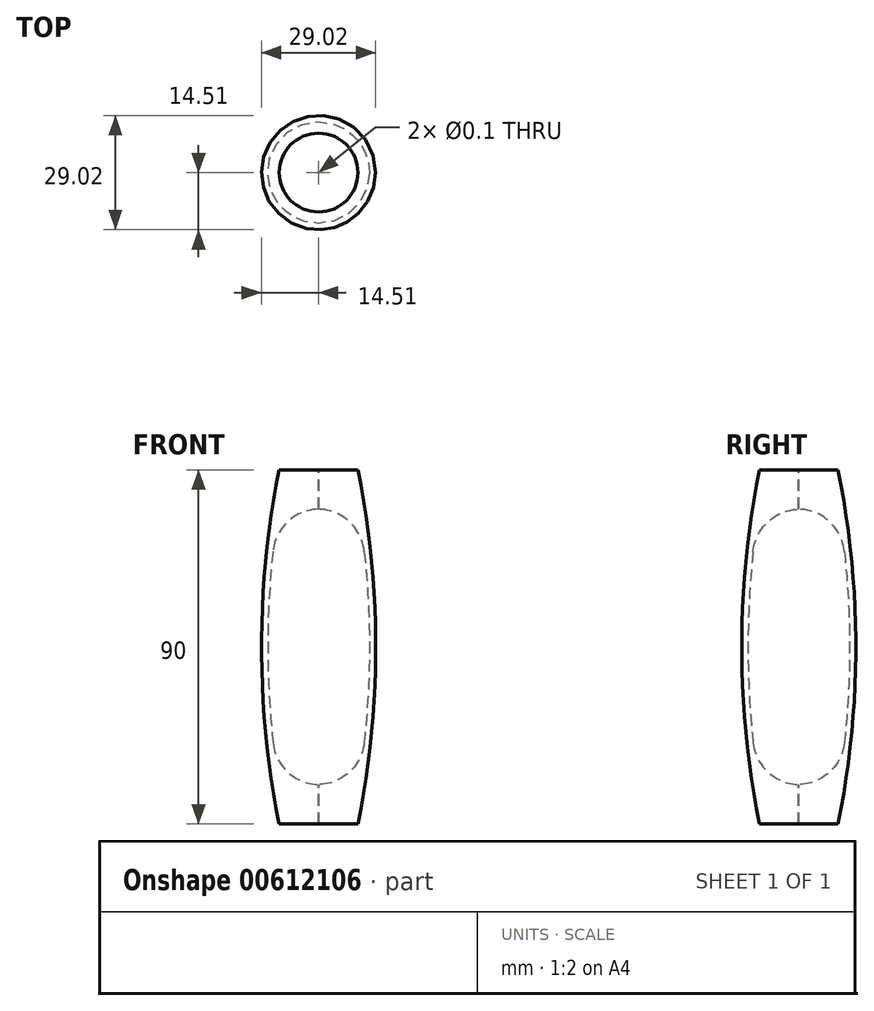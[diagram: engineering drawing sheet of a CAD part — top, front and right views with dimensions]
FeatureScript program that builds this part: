
annotation { "Feature Type Name" : "Feature", "Feature Type Description" : "" }
export const myFeature = defineFeature(function(context is Context, id is Id, definition is map)
    precondition{}
    {
        {
            var Q0;
            Q0=qCreatedBy(makeId("Front.planeOp"),FACE);
            var sketch = newSketch(context, id + "F0", { "sketchPlane" : qUnion([Q0])});
            skLineSegment(sketch, "E0", {"start": v(0, 45) * mm, "end": v(10, 45) * mm});
            skLineSegment(sketch, "E1", {"start": v(0, -45) * mm, "end": v(10, -45) * mm});
            skArc(sketch, "E2", {"start": v(10, 45) * mm, "mid": v(14.5, 0) * mm, "end": v(10, -45) * mm});
            skLineSegment(sketch, "E3", {"start": v(0, 45) * mm, "end": v(0, 35) * mm});
            skLineSegment(sketch, "E4", {"start": v(0, -35) * mm, "end": v(0, -45) * mm});
            skArc(sketch, "E5", {"start": v(0, 35) * mm, "mid": v(7.8, 31.82) * mm, "end": v(11.6, 24.3) * mm});
            skArc(sketch, "E6", {"start": v(0, -35) * mm, "mid": v(7.8, -31.82) * mm, "end": v(11.6, -24.3) * mm});
            skLineSegment(sketch, "E7", {"start": v(0, 35) * mm, "end": v(0, 0) * mm, "construction": true});
            skLineSegment(sketch, "E8", {"start": v(0, 0) * mm, "end": v(0, -35) * mm, "construction": true});
            skArc(sketch, "E9.0", {"start": v(11.6, 24.3) * mm, "mid": v(12.9, 0) * mm, "end": v(11.6, -24.3) * mm});
            skSolve(sketch);
        }
        {
            var Q0;
            Q0 = qSketchRegion(id + "F0", true);
            var Q1;
            Q1=sQuery(id+"F0.wireOp",EDGE,"E3");
            revolve(context, id + "F1", {"entities" : qUnion([Q0]), "axis" : qUnion([Q1]), "revolveType" : RevolveType.FULL});
        }
        {
            var Q0;
            Q0=makeQuery(id+"F1.opRevolve","SWEPT_FACE",FACE,{"disambiguationData":[OSD([sQuery(id+"F0.wireOp",EDGE,"E0")])]});
            var sketch = newSketch(context, id + "F2", { "sketchPlane" : qUnion([Q0])});
            skCircle(sketch, "E10", {"center": v(0, 0) * mm, "radius": 0.05 * mm});
            skSolve(sketch);
        }
        {
            var Q0;
            Q0 = qSketchRegion(id + "F2", true);
            extrude(context, id + "F3", {"entities" : qUnion([Q0]), "operationType" : NewBodyOperationType.REMOVE, "endBound" : BoundingType.THROUGH_ALL, "oppositeDirection" : true, "depth" : 25 * mm, "offsetDistance" : 25 * mm});
        }
    });
